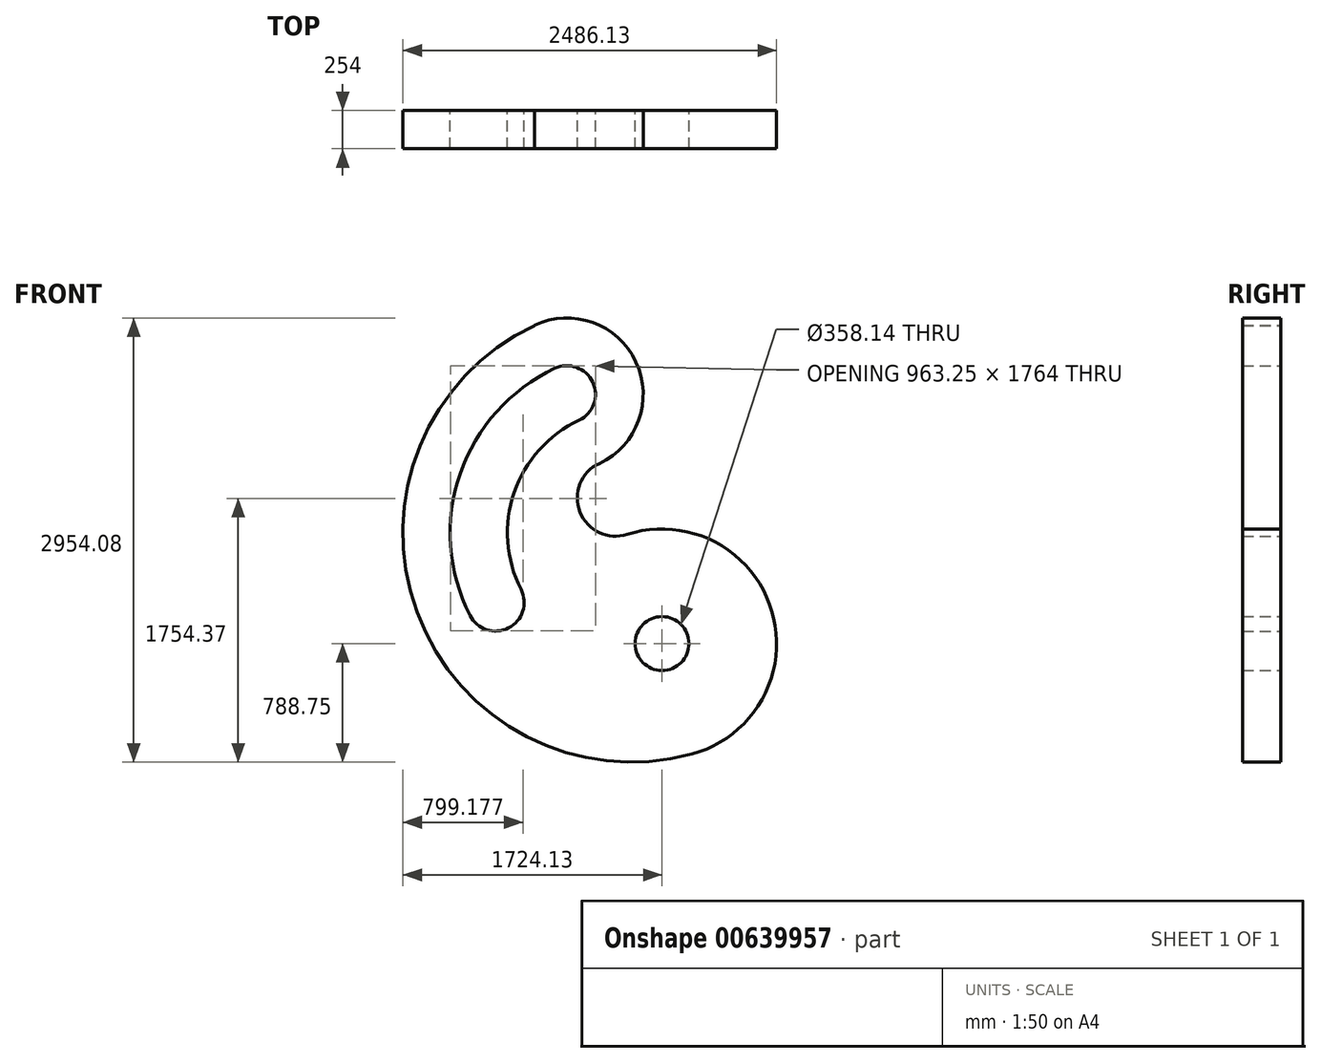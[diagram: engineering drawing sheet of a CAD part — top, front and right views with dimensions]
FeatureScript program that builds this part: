
annotation { "Feature Type Name" : "Feature", "Feature Type Description" : "" }
export const myFeature = defineFeature(function(context is Context, id is Id, definition is map)
    precondition{}
    {
        {
            var Q0;
            Q0=qCreatedBy(makeId("Front.planeOp"),FACE);
            var sketch = newSketch(context, id + "F0", { "sketchPlane" : qUnion([Q0])});
            skArc(sketch, "E0", {"start": v(200.13, -735.25) * mm, "mid": v(730.7, 216.16) * mm, "end": v(-232.07, 725.8) * mm});
            skCircle(sketch, "E1", {"center": v(0, 0) * mm, "radius": 179.07 * mm});
            skLineSegment(sketch, "E2", {"start": v(-849.75, 2117.06) * mm, "end": v(-848.51, 2114.44) * mm});
            skArc(sketch, "E3", {"start": v(-417.5, 1197.6) * mm, "mid": v(-539.3, 859.67) * mm, "end": v(-201.37, 737.87) * mm});
            skArc(sketch, "E4", {"start": v(-417.5, 1197.6) * mm, "mid": v(-188.99, 1903.02) * mm, "end": v(-907.83, 2084.97) * mm});
            skArc(sketch, "E5", {"start": v(-848.51, 2114.44) * mm, "mid": v(-1630.37, 208.94) * mm, "end": v(200.13, -735.25) * mm});
            skLineSegment(sketch, "E6.trimOffspring", {"start": v(-201.37, 737.87) * mm, "end": v(-200.13, 735.25) * mm});
            skPoint(sketch, "E7.trimOffspring.end.orphan", {"position": v(-1764.11, 0) * mm});
            skArc(sketch, "E8", {"start": v(-552.57, 1484.93) * mm, "mid": v(-461.22, 1738.38) * mm, "end": v(-714.67, 1829.73) * mm});
            skArc(sketch, "E9", {"start": v(-714.67, 1829.73) * mm, "mid": v(-1344.07, 1127.75) * mm, "end": v(-1278.24, 187.23) * mm});
            skArc(sketch, "E10", {"start": v(-1278.24, 187.23) * mm, "mid": v(-1022.1, 103.73) * mm, "end": v(-938.6, 359.87) * mm});
            skArc(sketch, "E11", {"start": v(-552.57, 1484.93) * mm, "mid": v(-983.69, 1004.1) * mm, "end": v(-938.6, 359.87) * mm});
            skSolve(sketch);
        }
        {
            var Q0;
            Q0=makeQuery(id+"F0.imprint","IMPRINT",FACE,{"disambiguationData":[TD([[makeQuery(id+"F0.imprint","IMPRINT",EDGE,{"derivedFrom":sQuery(id+"F0.wireOp",EDGE,"E1")}),-1.0]])]});
            extrude(context, id + "F1", {"entities" : qUnion([Q0]), "depth" : 254 * mm, "offsetDistance" : 25.4 * mm});
        }
    });
